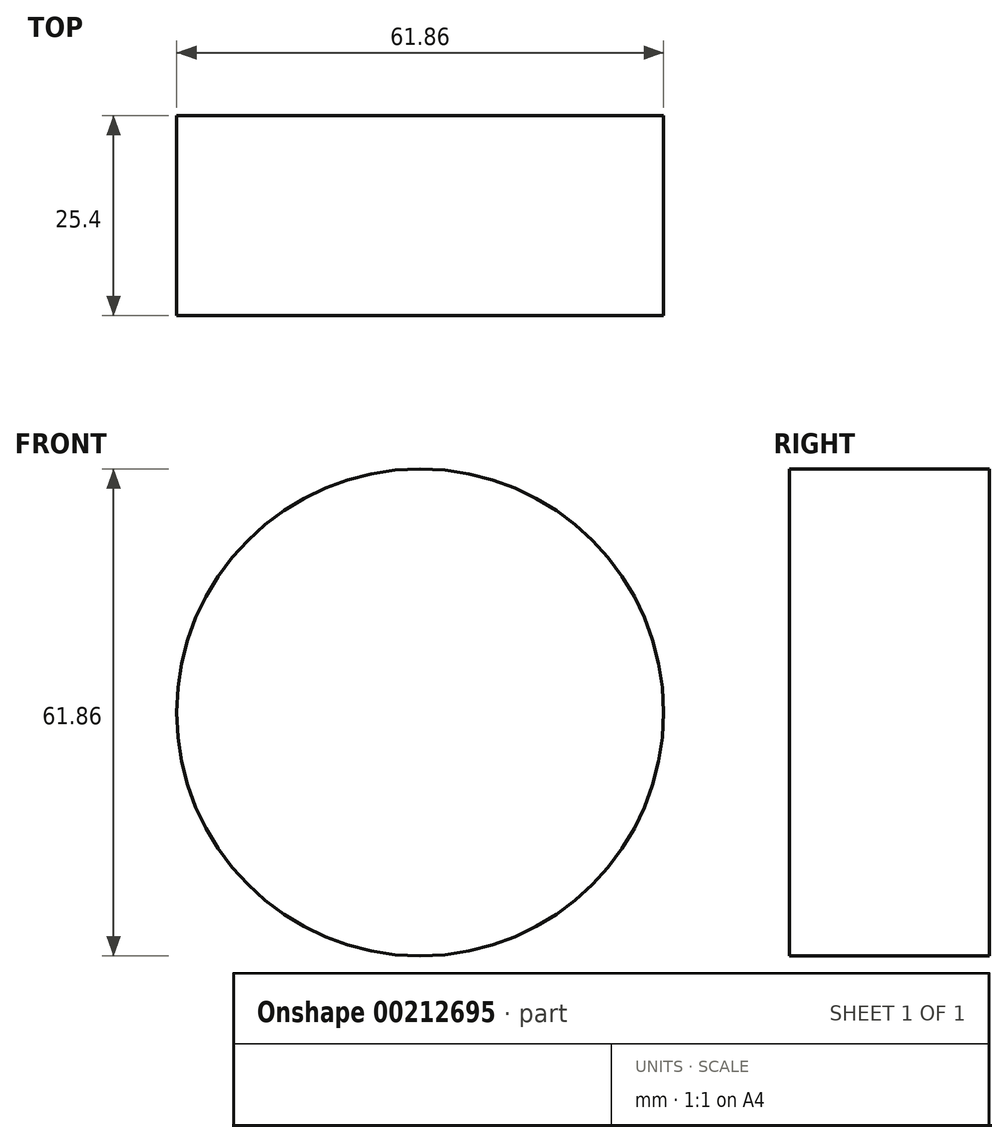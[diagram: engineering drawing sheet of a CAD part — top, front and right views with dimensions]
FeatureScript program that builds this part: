
annotation { "Feature Type Name" : "Feature", "Feature Type Description" : "" }
export const myFeature = defineFeature(function(context is Context, id is Id, definition is map)
    precondition{}
    {
        {
            var Q0;
            Q0=qCreatedBy(makeId("Front.planeOp"),FACE);
            var sketch = newSketch(context, id + "F0", { "sketchPlane" : qUnion([Q0])});
            skCircle(sketch, "E0", {"center": v(0, 0) * mm, "radius": 30.93 * mm});
            skSolve(sketch);
        }
        {
            var Q0;
            Q0=makeQuery(id+"F0.imprint","IMPRINT",FACE,{"disambiguationData":[TD([[makeQuery(id+"F0.imprint","IMPRINT",EDGE,{"derivedFrom":sQuery(id+"F0.wireOp",EDGE,"E0")}),1.0]])]});
            extrude(context, id + "F1", {"entities" : qUnion([Q0]), "depth" : 25.4 * mm});
        }
    });
